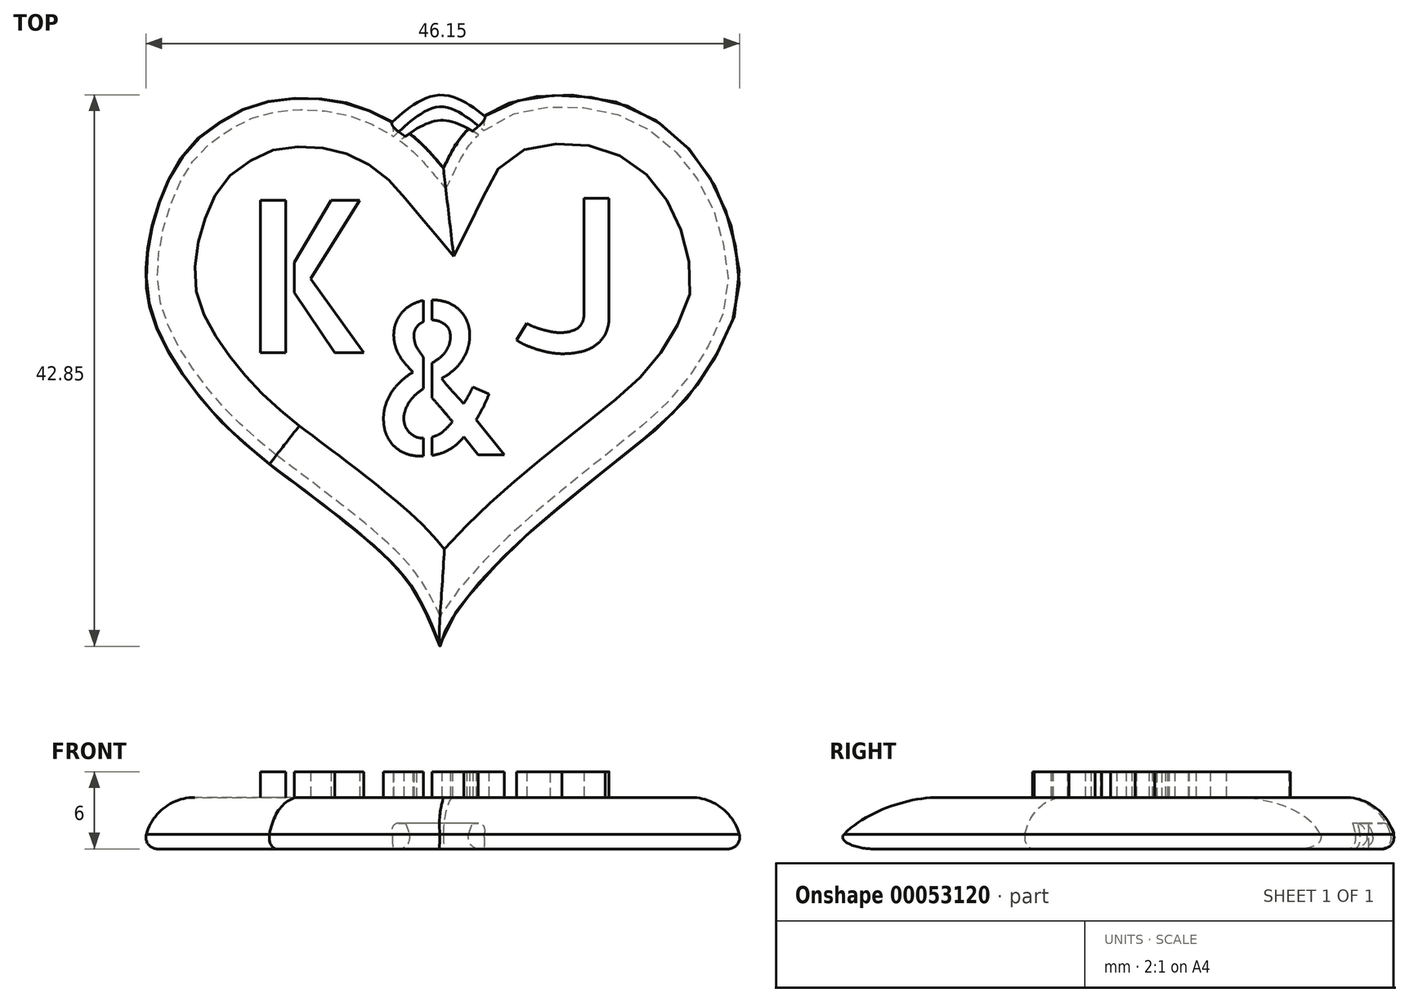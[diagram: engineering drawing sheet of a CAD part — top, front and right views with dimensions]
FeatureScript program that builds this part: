
annotation { "Feature Type Name" : "Feature", "Feature Type Description" : "" }
export const myFeature = defineFeature(function(context is Context, id is Id, definition is map)
    precondition{}
    {
        {
            var Q0;
            Q0=qCreatedBy(makeId("Top.planeOp"),FACE);
            var sketch = newSketch(context, id + "F0", { "sketchPlane" : qUnion([Q0])});
            skFitSpline(sketch, "E0", {"points": [v(15.47, -25.5) * mm, v(13.69, -21.5) * mm, v(10.96, -18.1) * mm, v(2.1, -11.09) * mm], "startDerivative": vector(-6.01, 15.18) * mm, "endDerivative": vector(-22.83, 17.04) * mm});
            skFitSpline(sketch, "E1", {"points": [v(15.47, -25.5) * mm, v(15.86, -24.18) * mm, v(17.3, -21.85) * mm, v(20.14, -18.64) * mm, v(24.42, -14.74) * mm, v(32.14, -8.49) * mm, v(33.77, -6.98) * mm, v(35.68, -4.71) * mm, v(37.45, -1.8) * mm, v(38.57, 0.95) * mm, v(38.84, 3.54) * mm, v(38.4, 6.61) * mm, v(37.54, 9.35) * mm, v(36.27, 11.74) * mm, v(34, 14.49) * mm, v(30.58, 16.76) * mm, v(26.95, 17.7) * mm, v(24, 17.8) * mm, v(21.3, 17.35) * mm, v(18.49, 15.93) * mm, v(16.8, 14.25) * mm, v(15.68, 12.24) * mm], "startDerivative": vector(9.05, 40.9) * mm, "endDerivative": vector(-25.96, -52.25) * mm});
            skFitSpline(sketch, "E2", {"points": [v(2.1, -11.09) * mm, v(-2.08, -7.28) * mm, v(-6.32, -1.25) * mm, v(-7.44, 2.4) * mm, v(-7.5, 4.11) * mm, v(-7.28, 6.43) * mm, v(-6.32, 9.84) * mm, v(-5.16, 12.26) * mm, v(-3.44, 14.4) * mm, v(-1.42, 15.86) * mm, v(0.4, 16.82) * mm, v(2.69, 17.42) * mm, v(4.8, 17.59) * mm, v(7.22, 17.39) * mm, v(9.34, 16.86) * mm, v(11.8, 15.7) * mm, v(13.98, 14.11) * mm, v(15.68, 12.24) * mm], "startDerivative": vector(-50.57, 41.47) * mm, "endDerivative": vector(29.44, -35.3) * mm});
            skSolve(sketch);
        }
        {
            var Q0;
            Q0 = qSketchRegion(id + "F0", true);
            extrude(context, id + "F1", {"entities" : qUnion([Q0]), "depth" : 4 * mm});
        }
        {
            var Q0;
            Q0=makeQuery(id+"F1.opExtrude","CAP_EDGE",EDGE,{"disambiguationData":[OSD([sQuery(id+"F0.wireOp",EDGE,"E1")])],"isStart":false});
            var Q1;
            Q1=makeQuery(id+"F1.opExtrude","CAP_EDGE",EDGE,{"disambiguationData":[OSD([sQuery(id+"F0.wireOp",EDGE,"E2")])],"isStart":false});
            var Q2;
            Q2=makeQuery(id+"F1.opExtrude","CAP_EDGE",EDGE,{"disambiguationData":[OSD([sQuery(id+"F0.wireOp",EDGE,"E0")])],"isStart":false});
            fillet(context, id + "F2", {"entities" : qUnion([Q0, Q1, Q2]), "radius" : 3.9 * mm, "tangentPropagation" : true, "allowEdgeOverflow" : false});
        }
        {
            var Q0;
            Q0=makeQuery(id+"F1.opExtrude","CAP_FACE",FACE,{"disambiguationData":[OSD([sQuery(id+"F0.wireOp",EDGE,"E0"),sQuery(id+"F0.wireOp",EDGE,"E1"),sQuery(id+"F0.wireOp",EDGE,"E2")])],"isStart":true});
            fillet(context, id + "F3", {"entities" : qUnion([Q0]), "radius" : 0.9 * mm, "tangentPropagation" : true, "allowEdgeOverflow" : false});
        }
        {
            var Q0;
            Q0=qCreatedBy(makeId("Top.planeOp"),FACE);
            var sketch = newSketch(context, id + "F4", { "sketchPlane" : qUnion([Q0])});
            skText(sketch, "E3", { "text": "K", "fontName": "AllertaStencil-Regular.ttf"});
            skText(sketch, "E4", { "text": "J", "fontName": "AllertaStencil-Regular.ttf"});
            skText(sketch, "E5", { "text": "&", "fontName": "AllertaStencil-Regular.ttf"});
            const initialGuessF4  = {"E3": [0, -0.00233, 1, 0, 0.01185], "E4": [0.02098, -0.00233, 1, 0, 0.01176], "E5": [0.00988, -0.01026, 1, 0, 0.01193]};
            skSetInitialGuess(sketch, initialGuessF4);
            skSolve(sketch);
        }
        {
            var Q0;
            Q0 = qSketchRegion(id + "F4", true);
            extrude(context, id + "F5", {"entities" : qUnion([Q0]), "operationType" : NewBodyOperationType.ADD, "depth" : 6 * mm});
        }
        {
            var Q0;
            Q0=qCreatedBy(makeId("Top.planeOp"),FACE);
            var sketch = newSketch(context, id + "F6", { "sketchPlane" : qUnion([Q0])});
            skLineSegment(sketch, "E6", {"start": v(15.64, 12.13) * mm, "end": v(15.64, 12.13) * mm});
            skLineSegment(sketch, "E7", {"start": v(20.1, 15.07) * mm, "end": v(20.1, 15.07) * mm});
            skLineSegment(sketch, "E8", {"start": v(20.1, 15.07) * mm, "end": v(19.13, 14.16) * mm});
            skLineSegment(sketch, "E9", {"start": v(11.75, 13.7) * mm, "end": v(10.64, 14.57) * mm});
            skFitSpline(sketch, "E10", {"points": [v(19.13, 14.16) * mm, v(15.5, 15.73) * mm, v(11.75, 13.7) * mm], "startDerivative": vector(-7.4, 4.95) * mm, "endDerivative": vector(-7.34, -5.78) * mm});
            skFitSpline(sketch, "E11", {"points": [v(20.1, 15.07) * mm, v(15.43, 17.7) * mm, v(10.64, 14.57) * mm], "startDerivative": vector(-9.5, 8.17) * mm, "endDerivative": vector(-9.41, -9.07) * mm});
            skSolve(sketch);
        }
        {
            var Q0;
            Q0 = qSketchRegion(id + "F6", true);
            extrude(context, id + "F7", {"entities" : qUnion([Q0]), "operationType" : NewBodyOperationType.ADD, "depth" : 2 * mm});
        }
        {
            var Q0;
            Q0=makeQuery(id+"F7.opExtrude","CAP_EDGE",EDGE,{"disambiguationData":[OSD([sQuery(id+"F6.wireOp",EDGE,"E11")])],"isStart":false});
            var Q1;
            Q1=makeQuery(id+"F7.opExtrude","CAP_EDGE",EDGE,{"disambiguationData":[OSD([sQuery(id+"F6.wireOp",EDGE,"E11")])],"isStart":true});
            fillet(context, id + "F8", {"entities" : qUnion([Q0, Q1]), "radius" : 0.9 * mm, "tangentPropagation" : true, "allowEdgeOverflow" : false});
        }
    });
